# Revit family: Armeret_BetonZig-Zag_45mm_p_i_t_1131106
name_source: partatom
category: Generic Models
units: mm (PartAtom-declared; Revit-internal decimal feet)

## family parameters
Always vertical = No
Can host rebar = No
Cut with Voids When Loaded = No
Part Type = Normal
Room Calculation Point = No
Round Connector Dimension = Use Diameter
Shared = No
Work Plane-Based = Yes

## types (13) — shared parameters
Default Elevation = 1219 mm
Technical Data Sheet = https://haucon.dk
Total Length = 800 mm  [stored 2.62467 ft]
Website Link = https://haucon.dk
concrete = Concrete

## per-type parameters (varying)
| type | Armerment Height | Armerment width |
| 35 mm | 35 mm | 35 mm |
| 55 mm | 55 mm | 55 mm |
| 40 mm | 40 mm | 40 mm |
| 45 mm | 45 mm  [stored 0.147638 ft] | 45 mm  [stored 0.147638 ft] |
| 50 mm | 50 mm | 50 mm |
| 60 mm | 60 mm | 60 mm |
| 25 mm | 25 mm  [stored 0.082021 ft] | 25 mm  [stored 0.082021 ft] |
| 30 mm | 30 mm  [stored 0.0984252 ft] | 30 mm  [stored 0.0984252 ft] |
| 70 mm | 70 mm | 70 mm |
| 75 mm | 75 mm | 75 mm |
| 80 mm | 80 mm | 80 mm |
| 90 mm | 90 mm | 90 mm |
| 100 mm | 100 mm  [stored 0.328084 ft] | 100 mm  [stored 0.328084 ft] |

note: [stored X ft] marks values corroborated as IEEE doubles in the binary element streams (Revit-internal decimal feet)

## geometry (parser evidence)
native form markers: Sweep x3
no freeform markers — native parametric forms only
